# Revit family: BLE-G-VDBW-G64-E26
name_source: partatom
category: Lighting Fixtures
units: mm (PartAtom-declared; Revit-internal decimal feet)

## family parameters
Cut with Voids When Loaded = No
Host = Face
Light Source = Yes
Maintain Annotation Orientation = No
Part Type = Normal
Room Calculation Point = No
Round Connector Dimension = Use Diameter
Shared = No

## types (12) — shared parameters
Base Material = 100 - Black
Color Filter = 16777215
Default Elevation = 4' - 0"
Dimming Lamp Color Temperature Shift = <None>
Gooseneck Material = 100 - Black
Photometric Web File = generic
Shade Material = 100 - Black
Tilt Angle = 0.00°

## per-type parameters (varying)
| type | 10" VC | 10" VS | 12" VC | 12" VS | 14" VC | 14" VS | 16" VC | 16" VS | 20" VC | 20" VS | 24" VC | 24" VS |
| 10" VS | No | Yes | No | No | No | No | No | No | No | No | No | No |
| 12" VC | No | No | Yes | No | No | No | No | No | No | No | No | No |
| 14" VC | No | No | No | No | Yes | No | No | No | No | No | No | No |
| 16" VC | No | No | No | No | No | No | Yes | No | No | No | No | No |
| 10" VC | Yes | No | No | No | No | No | No | No | No | No | No | No |
| 12" VS | No | No | No | Yes | No | No | No | No | No | No | No | No |
| 14" VS | No | No | No | No | No | Yes | No | No | No | No | No | No |
| 16" VS | No | Yes | No | No | No | No | No | Yes | No | No | No | No |
| 20" VC | No | No | No | No | No | No | No | No | Yes | No | No | No |
| 20" VS | No | No | No | No | No | No | No | No | No | Yes | No | No |
| 24" VC | No | No | No | No | No | No | No | No | No | No | Yes | No |
| 24" VS | No | No | No | No | No | No | No | No | No | No | No | Yes |

## geometry (parser evidence)
native form markers: Sweep x40
no freeform markers — native parametric forms only
